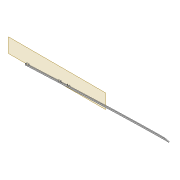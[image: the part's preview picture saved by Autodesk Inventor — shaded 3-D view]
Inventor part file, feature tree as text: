
AUTODESK INVENTOR PART (.ipt)
format: ipt  version: 2022 (Build 260153000, 153)  size: 570,368 bytes
history: native  units: mm
features: sketch x9, projected_geometry x9, extrude x8, fillet x2, shell x1, plane x1, chamfer x1
ambient origin geometry x8: Origin, YZ Plane, XZ Plane, XY Plane, X Axis, Y Axis, Z Axis, Center Point
bodies: Solid1 (feature_tree)
feature tree (31):
  extrude  "Extrusion1"  Depth=4.0mm
  shell  "Shell1"  Thickness=2.0mm
  extrude  "Extrusion8"  Depth=5.9mm
  extrude  "Extrusion3"  Depth=10.0mm TaperAngle=0.0deg
  extrude  "Extrusion4"  Depth=5.0mm
  fillet  "Fillet1"  Radius=5.0mm
  sketch  "Sketch10"  dims[d22=2.0mm d23=0.0mm d31=2.0mm d32=5.0mm]
  extrude  "Extrusion5"  Depth=2.5mm
  plane  "Work Plane2"
  extrude  "Extrusion9"  Depth=5.0mm
  fillet  "Fillet2"  Radius=2.5mm
  extrude  "Extrusion10"  Depth=6.0mm
  chamfer  "Chamfer1"  Distance=2.0mm
  extrude  "Extrusion12"  Depth=12.0mm
  sketch  "Sketch29"  dims[d66=3.0mm d67=12.0mm]
  sketch  "Sketch30"  dims[d68=5.0mm d69=10.0mm d70=12.0mm d71=3.05mm d72=10.0mm d73=0.0mm d74=2.0mm d75=100.0mm d76=20.0mm d77=0.5mm d78=10.0mm d79=0.0mm d82=3.0mm d83=2.0mm d84=45.0deg d85=1.0mm d86=1.0mm d87=1.0mm d88=1.0mm d89=1.0mm d90=1.0mm d91=10.0mm d92=0.0mm]
  sketch  "Sketch3"  dims[d0=2.0mm d1=0.0mm d2=4.0mm d7=2.0mm]
  sketch  "Sketch8"  dims[d8=2.0mm d9=5.9mm]
  sketch  "Sketch9"  dims[d13=10.0mm d14=0.0mm d16=10.0mm d17=0.0mm]
  projected_geometry  "Projected Loop4"
  projected_geometry  "Projected Loop10"
  sketch  "Sketch24"  dims[d34=1.6mm d35=2.5mm]
  projected_geometry  "Projected Loop11"
  projected_geometry  "Projected Loop12"
  projected_geometry  "Projected Loop13"
  sketch  "Sketch26"  dims[d37=5.0mm d38=1.6mm d40=2.5mm]
  projected_geometry  "Projected Loop14"
  sketch  "Sketch28"  dims[d62=80.0mm d63=6.0mm d64=2.0mm d65=0.0mm]
  projected_geometry  "Project Cut Edges1"
  projected_geometry  "Project Cut Edges2"
  projected_geometry  "Project Cut Edges3"
